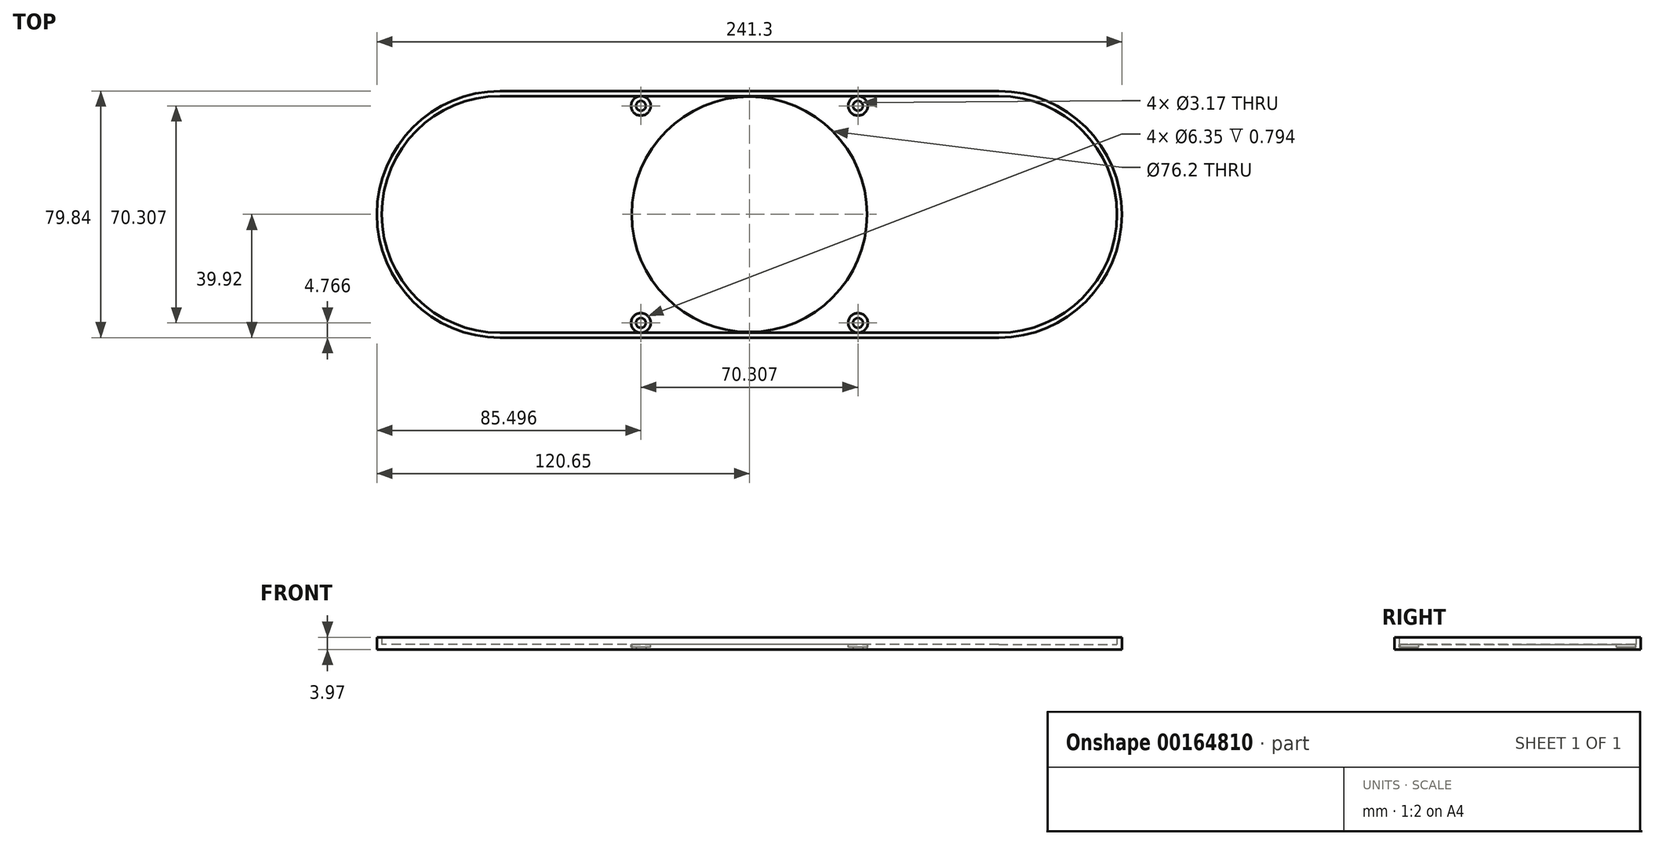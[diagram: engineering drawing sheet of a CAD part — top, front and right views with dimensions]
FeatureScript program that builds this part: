
annotation { "Feature Type Name" : "Feature", "Feature Type Description" : "" }
export const myFeature = defineFeature(function(context is Context, id is Id, definition is map)
    precondition{}
    {
        {
            var Q0;
            Q0=qCreatedBy(makeId("Top.planeOp"),FACE);
            var sketch = newSketch(context, id + "F0", { "sketchPlane" : qUnion([Q0])});
            skCircle(sketch, "E0", {"center": v(0, 0) * mm, "radius": 38.1 * mm});
            skLineSegment(sketch, "E1.bottom", {"start": v(-35.15, 35.15) * mm, "end": v(35.15, 35.15) * mm, "construction": true});
            skLineSegment(sketch, "E1.top", {"start": v(-35.15, -35.15) * mm, "end": v(35.15, -35.15) * mm, "construction": true});
            skLineSegment(sketch, "E1.left", {"start": v(-35.15, 35.15) * mm, "end": v(-35.15, -35.15) * mm, "construction": true});
            skLineSegment(sketch, "E1.right", {"start": v(35.15, 35.15) * mm, "end": v(35.15, -35.15) * mm, "construction": true});
            skCircle(sketch, "E2", {"center": v(-35.15, 35.15) * mm, "radius": 1.59 * mm});
            skCircle(sketch, "E3", {"center": v(-35.15, -35.15) * mm, "radius": 1.59 * mm});
            skCircle(sketch, "E4", {"center": v(35.15, -35.15) * mm, "radius": 1.59 * mm});
            skCircle(sketch, "E5", {"center": v(35.15, 35.15) * mm, "radius": 1.59 * mm});
            skCircle(sketch, "E6", {"center": v(35.15, -35.15) * mm, "radius": 3.18 * mm, "construction": true});
            skLineSegment(sketch, "E7.bottom", {"start": v(80.73, 39.92) * mm, "end": v(-80.73, 39.92) * mm});
            skLineSegment(sketch, "E7.top", {"start": v(80.73, -39.92) * mm, "end": v(-80.73, -39.92) * mm});
            skLineSegment(sketch, "E7.left", {"start": v(80.73, 39.92) * mm, "end": v(80.73, -39.92) * mm, "construction": true});
            skLineSegment(sketch, "E7.right", {"start": v(-80.73, 39.92) * mm, "end": v(-80.73, -39.92) * mm, "construction": true});
            skCircle(sketch, "E8", {"center": v(-35.15, 35.15) * mm, "radius": 4.76 * mm, "construction": true});
            skArc(sketch, "E9", {"start": v(-80.73, 39.92) * mm, "mid": v(-120.65, 0) * mm, "end": v(-80.73, -39.92) * mm});
            skArc(sketch, "E10", {"start": v(80.73, -39.92) * mm, "mid": v(120.65, 0) * mm, "end": v(80.73, 39.92) * mm});
            skSolve(sketch);
        }
        {
            var Q0;
            Q0=qSketchRegion(id+"F0",true);
            extrude(context, id + "F1", {"entities" : qUnion([Q0]), "depth" : 1.59 * mm});
        }
        {
            var Q0;
            Q0=makeQuery(id+"F1.opExtrude","CAP_FACE",FACE,{"disambiguationData":[OSD([sQuery(id+"F0.wireOp",EDGE,"6DVzzu6l-ey9Q-ONbp-tjIE-3zeTyLKKNsiZ"),sQuery(id+"F0.wireOp",EDGE,"E0"),sQuery(id+"F0.wireOp",EDGE,"E2"),sQuery(id+"F0.wireOp",EDGE,"E3"),sQuery(id+"F0.wireOp",EDGE,"E4"),sQuery(id+"F0.wireOp",EDGE,"E5")])],"isStart":false});
            var sketch = newSketch(context, id + "F2", { "sketchPlane" : qUnion([Q0])});
            skArc(sketch, "E11", {"start": v(-80.73, 39.92) * mm, "mid": v(-120.65, 0) * mm, "end": v(-80.73, -39.92) * mm});
            skArc(sketch, "E12", {"start": v(80.73, -39.92) * mm, "mid": v(120.65, 0) * mm, "end": v(80.73, 39.92) * mm});
            skLineSegment(sketch, "E13", {"start": v(-80.73, 39.92) * mm, "end": v(80.73, 39.92) * mm});
            skLineSegment(sketch, "E14", {"start": v(80.73, -39.92) * mm, "end": v(-80.73, -39.92) * mm});
            skLineSegment(sketch, "E15", {"start": v(-80.73, 39.92) * mm, "end": v(-80.73, 38.33) * mm, "construction": true});
            skLineSegment(sketch, "E16", {"start": v(80.73, -39.92) * mm, "end": v(80.73, -38.33) * mm, "construction": true});
            skLineSegment(sketch, "E17.bottom", {"start": v(80.73, -38.33) * mm, "end": v(-80.73, -38.33) * mm});
            skLineSegment(sketch, "E17.top", {"start": v(80.73, 38.33) * mm, "end": v(-80.73, 38.33) * mm});
            skLineSegment(sketch, "E17.left", {"start": v(80.73, -38.33) * mm, "end": v(80.73, 38.33) * mm, "construction": true});
            skLineSegment(sketch, "E17.right", {"start": v(-80.73, -38.33) * mm, "end": v(-80.73, 38.33) * mm, "construction": true});
            skPoint(sketch, "E17.middle", {"position": v(0, 0) * mm});
            skArc(sketch, "E18", {"start": v(-80.73, 38.33) * mm, "mid": v(-119.06, 0) * mm, "end": v(-80.73, -38.33) * mm});
            skArc(sketch, "E19", {"start": v(80.73, -38.33) * mm, "mid": v(119.06, 0) * mm, "end": v(80.73, 38.33) * mm});
            skSolve(sketch);
        }
        {
            var Q0;
            Q0=qSketchRegion(id+"F2",true);
            extrude(context, id + "F3", {"entities" : qUnion([Q0]), "operationType" : NewBodyOperationType.ADD, "depth" : 2.38 * mm});
        }
        {
            var Q0;
            Q0=makeQuery(id+"F1.opExtrude","CAP_FACE",FACE,{"disambiguationData":[OSD([sQuery(id+"F0.wireOp",EDGE,"6DVzzu6l-ey9Q-ONbp-tjIE-3zeTyLKKNsiZ"),sQuery(id+"F0.wireOp",EDGE,"E0"),sQuery(id+"F0.wireOp",EDGE,"E2"),sQuery(id+"F0.wireOp",EDGE,"E3"),sQuery(id+"F0.wireOp",EDGE,"E4"),sQuery(id+"F0.wireOp",EDGE,"E5")])],"isStart":false});
            var sketch = newSketch(context, id + "F4", { "sketchPlane" : qUnion([Q0])});
            skCircle(sketch, "E20", {"center": v(-35.15, 35.15) * mm, "radius": 3.18 * mm});
            skCircle(sketch, "E21", {"center": v(35.15, 35.15) * mm, "radius": 3.18 * mm});
            skCircle(sketch, "E22", {"center": v(35.15, -35.15) * mm, "radius": 3.18 * mm});
            skCircle(sketch, "E23", {"center": v(-35.15, -35.15) * mm, "radius": 3.17 * mm});
            skSolve(sketch);
        }
        {
            var Q0;
            Q0=qSketchRegion(id+"F4",true);
            extrude(context, id + "F5", {"entities" : qUnion([Q0]), "operationType" : NewBodyOperationType.REMOVE, "oppositeDirection" : true, "depth" : 0.8 * mm});
        }
    });
